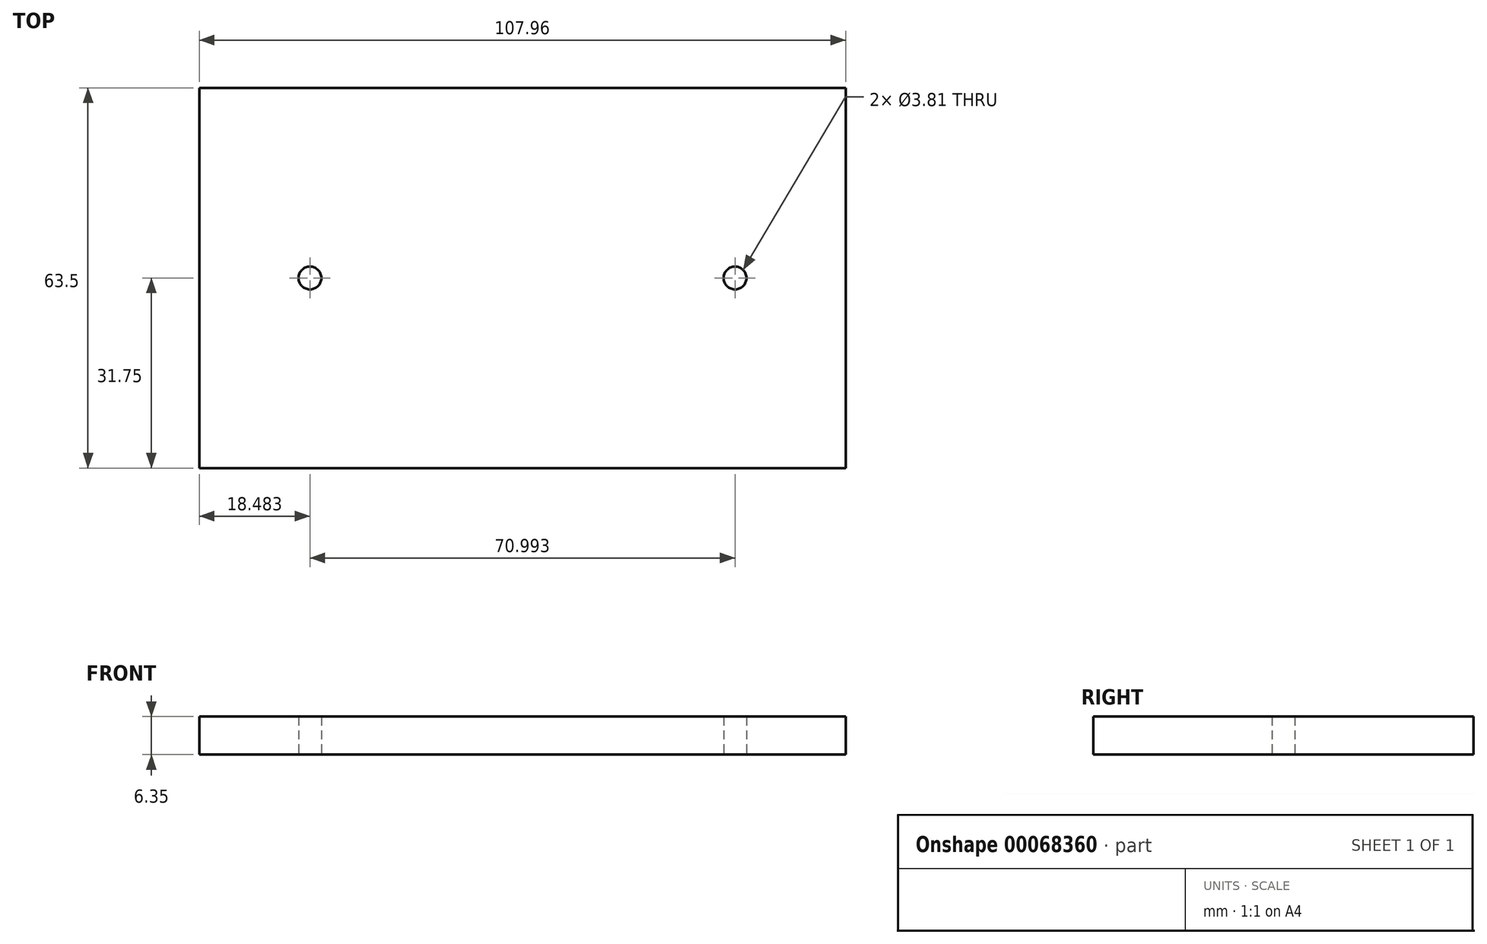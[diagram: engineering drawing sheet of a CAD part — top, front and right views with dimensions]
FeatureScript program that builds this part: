
annotation { "Feature Type Name" : "Feature", "Feature Type Description" : "" }
export const myFeature = defineFeature(function(context is Context, id is Id, definition is map)
    precondition{}
    {
        {
            var Q0;
            Q0=qCreatedBy(makeId("Top.planeOp"),FACE);
            var sketch = newSketch(context, id + "F0", { "sketchPlane" : qUnion([Q0])});
            skLineSegment(sketch, "E0.bottom", {"start": v(35.5, 18.53) * mm, "end": v(-35.5, 18.53) * mm});
            skLineSegment(sketch, "E0.top", {"start": v(35.5, -18.53) * mm, "end": v(-35.5, -18.53) * mm});
            skLineSegment(sketch, "E0.left", {"start": v(35.5, 18.53) * mm, "end": v(35.5, -18.53) * mm});
            skLineSegment(sketch, "E0.right", {"start": v(-35.5, 18.53) * mm, "end": v(-35.5, -18.53) * mm});
            skPoint(sketch, "E0.middle", {"position": v(0, 0) * mm});
            skCircle(sketch, "E1", {"center": v(-35.5, 0) * mm, "radius": 1.9 * mm});
            skCircle(sketch, "E2", {"center": v(35.5, 0) * mm, "radius": 1.9 * mm});
            skLineSegment(sketch, "E3.bottom", {"start": v(53.98, 31.75) * mm, "end": v(-53.97, 31.75) * mm});
            skLineSegment(sketch, "E3.top", {"start": v(53.98, -31.75) * mm, "end": v(-53.97, -31.75) * mm});
            skLineSegment(sketch, "E3.left", {"start": v(53.98, 31.75) * mm, "end": v(53.98, -31.75) * mm});
            skLineSegment(sketch, "E3.right", {"start": v(-53.97, 31.75) * mm, "end": v(-53.97, -31.75) * mm});
            skSolve(sketch);
        }
        {
            var Q0;
            {var subQ8=sQuery(id+"F0.wireOp",EDGE,"E0.bottom");Q0=makeQuery(id+"F0.imprint","IMPRINT",FACE,{"disambiguationData":[TD([[makeQuery(id+"F0.imprint","IMPRINT",EDGE,{"derivedFrom":subQ8}),-1.0]])]});}
            var Q1;
            {var subQ4=sQuery(id+"F0.wireOp",EDGE,"E0.bottom");Q1=makeQuery(id+"F0.imprint","IMPRINT",FACE,{"disambiguationData":[TD([[makeQuery(id+"F0.imprint","IMPRINT",EDGE,{"derivedFrom":subQ4}),1.0]])]});}
            extrude(context, id + "F1", {"entities" : qUnion([Q0, Q1]), "depth" : 6.35 * mm});
        }
    });
